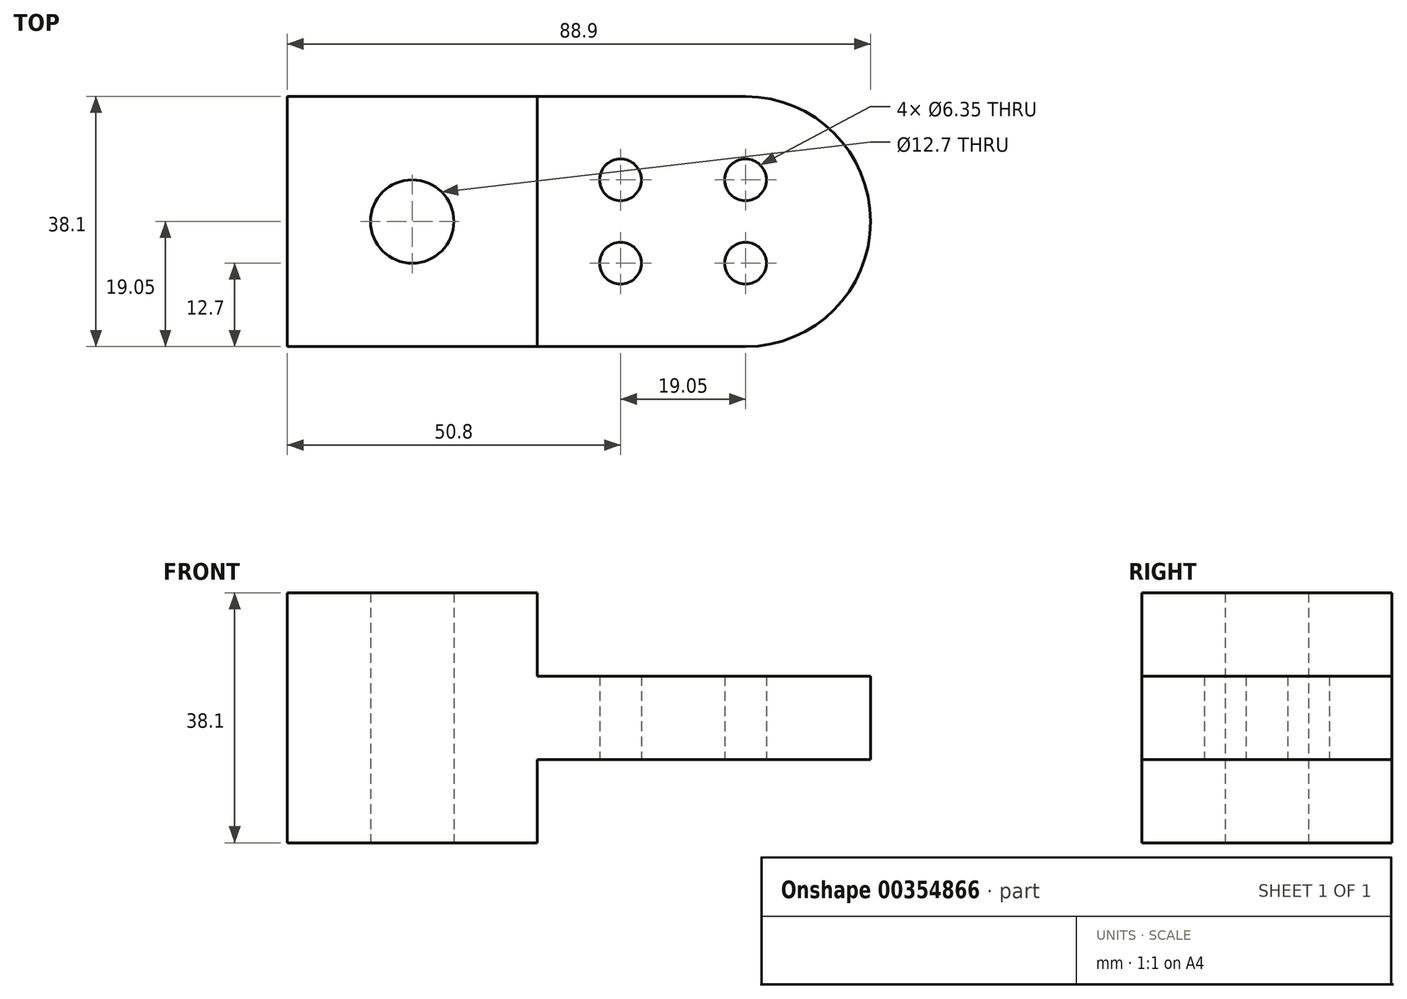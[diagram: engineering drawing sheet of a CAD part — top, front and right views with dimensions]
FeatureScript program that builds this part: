
annotation { "Feature Type Name" : "Feature", "Feature Type Description" : "" }
export const myFeature = defineFeature(function(context is Context, id is Id, definition is map)
    precondition{}
    {
        {
            var Q0;
            Q0=qCreatedBy(makeId("Top.planeOp"),FACE);
            var sketch = newSketch(context, id + "F0", { "sketchPlane" : qUnion([Q0])});
            skLineSegment(sketch, "E0.bottom", {"start": v(-19.05, 19.05) * mm, "end": v(19.05, 19.05) * mm});
            skLineSegment(sketch, "E0.top", {"start": v(-19.05, -19.05) * mm, "end": v(19.05, -19.05) * mm});
            skLineSegment(sketch, "E0.left", {"start": v(-19.05, 19.05) * mm, "end": v(-19.05, -19.05) * mm});
            skLineSegment(sketch, "E0.right", {"start": v(19.05, 19.05) * mm, "end": v(19.05, -19.05) * mm});
            skCircle(sketch, "E1", {"center": v(0, 0) * mm, "radius": 6.35 * mm});
            skSolve(sketch);
        }
        {
            var Q0;
            Q0 = qSketchRegion(id + "F0", true);
            extrude(context, id + "F1", {"entities" : qUnion([Q0]), "endBound" : BoundingType.SYMMETRIC, "depth" : 38.1 * mm});
        }
        {
            var Q0;
            Q0=qCreatedBy(makeId("Top.planeOp"),FACE);
            var sketch = newSketch(context, id + "F2", { "sketchPlane" : qUnion([Q0])});
            skLineSegment(sketch, "E2", {"start": v(19.05, 19.05) * mm, "end": v(19.05, -19.05) * mm});
            skLineSegment(sketch, "E3", {"start": v(19.05, -19.05) * mm, "end": v(50.8, -19.05) * mm});
            skArc(sketch, "E4", {"start": v(50.8, -19.05) * mm, "mid": v(69.85, 0) * mm, "end": v(50.8, 19.05) * mm});
            skLineSegment(sketch, "E5", {"start": v(50.8, 19.05) * mm, "end": v(19.05, 19.05) * mm});
            skCircle(sketch, "E6", {"center": v(31.75, 6.35) * mm, "radius": 3.18 * mm});
            skCircle(sketch, "E7", {"center": v(50.8, 6.35) * mm, "radius": 3.18 * mm});
            skCircle(sketch, "E8", {"center": v(31.75, -6.35) * mm, "radius": 3.18 * mm});
            skCircle(sketch, "E9", {"center": v(50.8, -6.35) * mm, "radius": 3.18 * mm});
            skSolve(sketch);
        }
        {
            var Q0;
            Q0 = qSketchRegion(id + "F2", true);
            extrude(context, id + "F3", {"entities" : qUnion([Q0]), "operationType" : NewBodyOperationType.ADD, "endBound" : BoundingType.SYMMETRIC, "depth" : 12.7 * mm});
        }
    });
